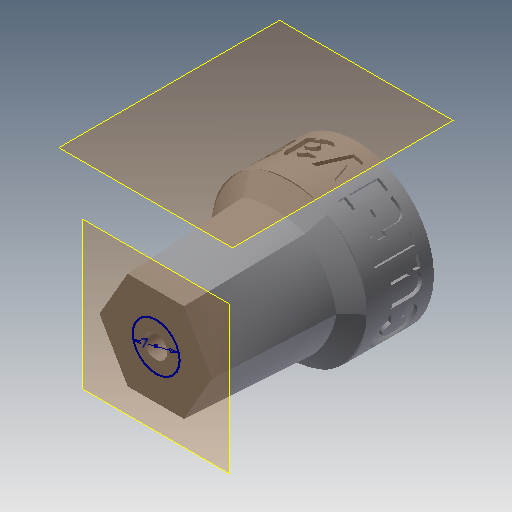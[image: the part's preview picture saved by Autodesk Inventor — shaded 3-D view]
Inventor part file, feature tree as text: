
AUTODESK INVENTOR PART (.ipt)
format: ipt  version: 2017 (Build 210142000, 142)  size: 698,880 bytes
history: native  units: mm
features: sketch x9, extrude x4, plane x2, projected_geometry x2, loft x1, chamfer x1, emboss x1
ambient origin geometry x8: Origin, YZ Plane, XZ Plane, XY Plane, X Axis, Y Axis, Z Axis, Center Point
bodies: Body1 (feature_tree)
feature tree (20):
  sketch  "Sketch3"  dims[d4=20.0mm d5=30.0mm]
  plane  "Work Plane1"
  loft  "Loft1"
  extrude  "Extrusion2"  TaperAngle=0.0deg  [1 undecoded]
  extrude  "Extrusion3"  Depth=20.0mm TaperAngle=0.0deg
  chamfer  "Chamfer1"  Distance=10.0mm
  sketch  "Sketch8"  dims[d23=0.5mm d24=0.0mm d25=10.0mm d26=0.0mm]
  plane  "Work Plane2"
  emboss  "Emboss1"
  extrude  "Extrusion4"  Depth=20.0mm
  sketch  "Sketch11"  dims[d29=20.0mm d30=0.0mm]
  extrude  "Extrusion5"  Depth=10.0mm TaperAngle=0.0deg
  sketch  "Sketch4"  dims[d6=0.0mm d7=90.0deg d8=0.0mm d9=90.0deg]
  sketch  "Sketch6"  dims[d13=3.4mm d14=20.0mm d15=0.0mm d16=10.0mm d17=0.0mm]
  sketch  "Sketch7"  dims[d19=2.3mm d20=2.0mm d21=45.0deg d22=20.0mm]
  projected_geometry  "Projected Loop1"
  sketch  "Sketch9"  dims[d27=7.0mm]
  sketch  "Sketch10"  dims[d28=7.0mm]
  projected_geometry  "Projected Loop2"
  sketch  "Sketch12"
note: 1 required parameter value undecoded (feature->parameter linkage not recoverable at this tier; creation-order binding heuristic only, values carry confidence <= 0.55)
